# Revit family: P6048B1T.V2,2T,1B,2B
name_source: partatom
category: Plumbing Fixtures
revit_build: Autodesk Revit LT 2016 (Build: 20160525_1230(x64)
units: mm (PartAtom-declared; Revit-internal decimal feet)

## family parameters
Always vertical = Yes
Cut with Voids When Loaded = No
OmniClass Number = 23.45.05.14.17
OmniClass Title = Showers
Part Type = Normal
Room Calculation Point = No
Round Connector Dimension = Use Diameter
Shared = No
Work Plane-Based = No

## types (4) — shared parameters
Assembly Code = D2010710
Keynote = 22 40 00.B3
Manufacturer = best bath
Type Comments = Barrier Free
URL = http://www.bestbath.com
Unit Depth = 49"
Unit Width = 60"

## per-type parameters (varying)
| type | Description | Threshold Height | Unit Height |
| P6048B1B.V2 | Shower Pan, Beveled Threshold | 1" | 6" |
| P6048B2B.V2 | Shower Pan, Beveled Threshold | 2" | 7" |
| P6048B1T.V2 | Shower Pan, Traditional Bull Nose Threshold | 1" | 6" |
| P6048B2T.V2 | Shower Pan, Traditional Bull Nose Threshold | 2" | 7" |

note: column(s) folded — value = type name in every type: Model

## geometry (parser evidence)
native form markers: Blend x20, Sweep x2
no freeform markers — native parametric forms only
